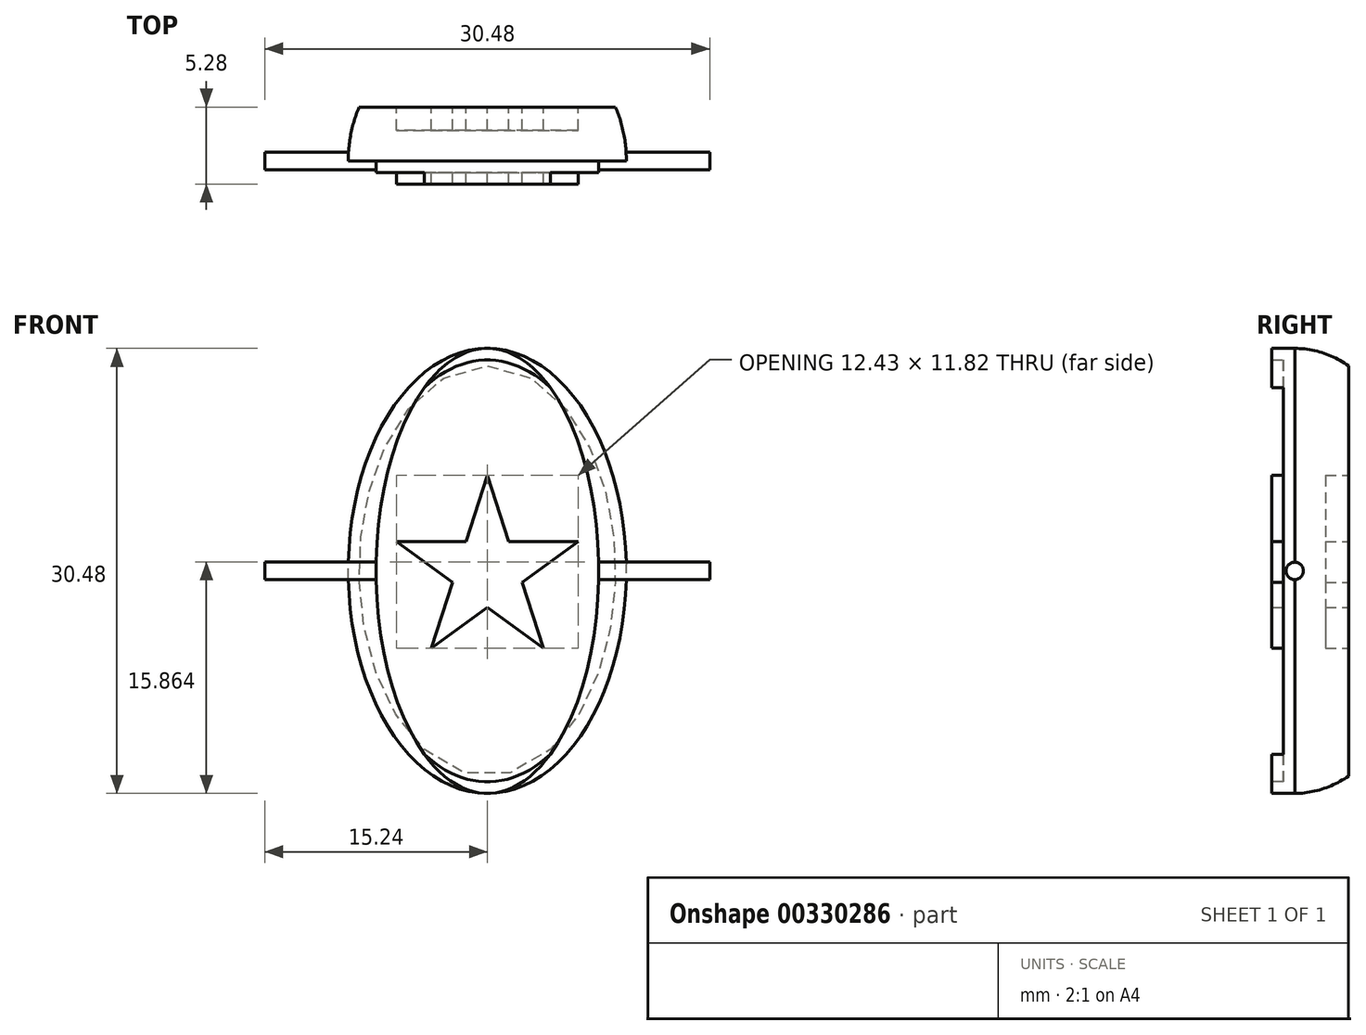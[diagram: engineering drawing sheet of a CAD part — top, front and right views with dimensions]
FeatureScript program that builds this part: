
annotation { "Feature Type Name" : "Feature", "Feature Type Description" : "" }
export const myFeature = defineFeature(function(context is Context, id is Id, definition is map)
    precondition{}
    {
        {
            var Q0;
            Q0=qCreatedBy(makeId("Front.planeOp"),FACE);
            var sketch = newSketch(context, id + "F0", { "sketchPlane" : qUnion([Q0])});
            skEllipticalArc(sketch, "E0", {});
            skLineSegment(sketch, "E1", {"start": v(0, 15.24) * mm, "end": v(0, -15.24) * mm});
            const initialGuessF0  = {"E0": [0, 0, 0, 1, 0.01524, 0.009525, 3.141592653589793, 0]};
            skSetInitialGuess(sketch, initialGuessF0);
            skSolve(sketch);
        }
        {
            var Q0;
            Q0=qSketchRegion(id+"F0",true);
            var Q1;
            Q1=sQuery(id+"F0.wireOp",EDGE,"E1");
            revolve(context, id + "F1", {"entities" : qUnion([Q0]), "axis" : qUnion([Q1]), "revolveType" : RevolveType.ONE_DIRECTION, "oppositeDirection" : true, "angle" : 180 * degree});
        }
        {
            var Q0;
            Q0=qCreatedBy(makeId("Right.planeOp"),FACE);
            var sketch = newSketch(context, id + "F2", { "sketchPlane" : qUnion([Q0])});
            skLineSegment(sketch, "E2.bottom", {"start": v(3.69, 15.9) * mm, "end": v(30.72, 15.9) * mm});
            skLineSegment(sketch, "E2.top", {"start": v(3.69, -22.6) * mm, "end": v(30.72, -22.6) * mm});
            skLineSegment(sketch, "E2.left", {"start": v(3.69, 15.9) * mm, "end": v(3.69, -22.6) * mm});
            skLineSegment(sketch, "E2.right", {"start": v(30.72, 15.9) * mm, "end": v(30.72, -22.6) * mm});
            skSolve(sketch);
        }
        {
            var Q0;
            Q0=qSketchRegion(id+"F2",true);
            extrude(context, id + "F3", {"entities" : qUnion([Q0]), "operationType" : NewBodyOperationType.REMOVE, "oppositeDirection" : true, "depth" : 25.4 * mm, "symmetric" : true});
        }
        {
            var Q0;
            Q0=qCreatedBy(makeId("Right.planeOp"),FACE);
            var sketch = newSketch(context, id + "F4", { "sketchPlane" : qUnion([Q0])});
            skCircle(sketch, "E3", {"center": v(0, 0) * mm, "radius": 0.6 * mm});
            skSolve(sketch);
        }
        {
            var Q0;
            Q0=makeQuery(id+"F1.opRevolve","CAP_FACE",FACE,{"disambiguationData":[OSD([sQuery(id+"F0.wireOp",EDGE,"E0"),sQuery(id+"F0.wireOp",EDGE,"E1")])],"isStart":false});
            var sketch = newSketch(context, id + "F5", { "sketchPlane" : qUnion([Q0])});
            skEllipticalArc(sketch, "E4.0", {});
            skEllipticalArc(sketch, "E4.1", {});
            const initialGuessF5  = {"E4.0": [0, 0, 0, 1, 0.01524, 0.00762, 0, 3.141592653589793], "E4.1": [0, 0, 0, 1, 0.01524, 0.00762, 3.141592653589793, 0]};
            skSetInitialGuess(sketch, initialGuessF5);
            skSolve(sketch);
        }
        {
            var Q0;
            Q0=qSketchRegion(id+"F5",true);
            extrude(context, id + "F6", {"entities" : qUnion([Q0]), "operationType" : NewBodyOperationType.ADD, "depth" : 1.59 * mm});
        }
        {
            var Q0;
            Q0=qSketchRegion(id+"F4",true);
            extrude(context, id + "F7", {"entities" : qUnion([Q0]), "operationType" : NewBodyOperationType.ADD, "depth" : 30.48 * mm, "symmetric" : true});
        }
        {
            var Q0;
            Q0=makeQuery(id+"F6.opExtrude","CAP_FACE",FACE,{"disambiguationData":[OSD([sQuery(id+"F5.wireOp",EDGE,"E4.0"),sQuery(id+"F5.wireOp",EDGE,"E4.1")])],"isStart":false});
            var sketch = newSketch(context, id + "F8", { "sketchPlane" : qUnion([Q0])});
            skEllipse(sketch, "E5", {"center": v(0, 0) * mm, "majorRadius": 14.45 * mm, "minorRadius": 8.73 * mm, "majorAxis": v(0, 1)});
            skSolve(sketch);
        }
        {
            var Q0;
            Q0=qSketchRegion(id+"F8",true);
            extrude(context, id + "F9", {"entities" : qUnion([Q0]), "operationType" : NewBodyOperationType.REMOVE, "oppositeDirection" : true, "depth" : 0.8 * mm});
        }
        {
            var Q0;
            Q0=makeQuery(id+"F9.boolean.opBoolean","COPY",FACE,{"derivedFrom":makeQuery(id+"F9.opExtrude","CAP_FACE",FACE,{"disambiguationData":[OSD([sQuery(id+"F8.wireOp",EDGE,"E5")])],"isStart":false})});
            var sketch = newSketch(context, id + "F10", { "sketchPlane" : qUnion([Q0])});
            skSolve(sketch);
        }
        {
            var Q0;
            Q0=makeQuery(id+"F10.imprint","IMPRINT",FACE,{"disambiguationData":[TD([[makeQuery(id+"F10.imprint","IMPRINT",EDGE,{"derivedFrom":makeQuery(id+"F9.boolean.opBoolean","COPY",EDGE,{"derivedFrom":makeQuery(id+"F9.opExtrude","CAP_EDGE",EDGE,{"disambiguationData":[OSD([sQuery(id+"F8.wireOp",EDGE,"E5")])],"isStart":false})})}),1.0]])]});
            var sketch = newSketch(context, id + "F11", { "sketchPlane" : qUnion([Q0])});
            skLineSegment(sketch, "E6", {"start": v(3.84, -5.29) * mm, "end": v(2.37, -0.77) * mm});
            skLineSegment(sketch, "E7", {"start": v(0, 6.53) * mm, "end": v(-1.47, 2.02) * mm});
            skLineSegment(sketch, "E8", {"start": v(-3.84, -5.29) * mm, "end": v(0, -2.5) * mm});
            skLineSegment(sketch, "E9", {"start": v(6.21, 2.02) * mm, "end": v(1.47, 2.02) * mm});
            skLineSegment(sketch, "E10", {"start": v(-6.21, 2.02) * mm, "end": v(-2.37, -0.77) * mm});
            skLineSegment(sketch, "E11.trimOffspring", {"start": v(-1.47, 2.02) * mm, "end": v(-6.21, 2.02) * mm});
            skLineSegment(sketch, "E12.trimOffspring", {"start": v(-2.37, -0.77) * mm, "end": v(-3.84, -5.29) * mm});
            skLineSegment(sketch, "E13.trimOffspring", {"start": v(0, -2.5) * mm, "end": v(3.84, -5.29) * mm});
            skLineSegment(sketch, "E14.trimOffspring", {"start": v(2.37, -0.77) * mm, "end": v(6.21, 2.02) * mm});
            skLineSegment(sketch, "E15.trimOffspring", {"start": v(1.47, 2.02) * mm, "end": v(0, 6.53) * mm});
            skSolve(sketch);
        }
        {
            var Q0;
            Q0=qSketchRegion(id+"F11",true);
            extrude(context, id + "F12", {"entities" : qUnion([Q0]), "operationType" : NewBodyOperationType.ADD, "depth" : 0.8 * mm});
        }
        {
            var Q0;
            Q0=makeQuery(id+"F3.boolean.opBoolean","COPY",FACE,{"derivedFrom":makeQuery(id+"F3.opExtrude","SWEPT_FACE",FACE,{"disambiguationData":[OSD([sQuery(id+"F2.wireOp",EDGE,"E2.left")])]})});
            var sketch = newSketch(context, id + "F13", { "sketchPlane" : qUnion([Q0])});
            skLineSegment(sketch, "E16.0", {"start": v(2.37, -0.77) * mm, "end": v(3.84, -5.29) * mm});
            skLineSegment(sketch, "E16.1", {"start": v(3.84, -5.29) * mm, "end": v(0, -2.5) * mm});
            skLineSegment(sketch, "E16.2", {"start": v(0, -2.5) * mm, "end": v(-3.84, -5.29) * mm});
            skLineSegment(sketch, "E16.3", {"start": v(-3.84, -5.29) * mm, "end": v(-2.37, -0.77) * mm});
            skLineSegment(sketch, "E16.4", {"start": v(-2.37, -0.77) * mm, "end": v(-6.21, 2.02) * mm});
            skLineSegment(sketch, "E16.5", {"start": v(-6.21, 2.02) * mm, "end": v(-1.47, 2.02) * mm});
            skLineSegment(sketch, "E16.6", {"start": v(-1.47, 2.02) * mm, "end": v(0, 6.53) * mm});
            skLineSegment(sketch, "E16.7", {"start": v(0, 6.53) * mm, "end": v(1.47, 2.02) * mm});
            skLineSegment(sketch, "E16.8", {"start": v(1.47, 2.02) * mm, "end": v(6.21, 2.02) * mm});
            skLineSegment(sketch, "E16.9", {"start": v(6.21, 2.02) * mm, "end": v(2.37, -0.77) * mm});
            skSolve(sketch);
        }
        {
            var Q0;
            Q0=qSketchRegion(id+"F13",true);
            extrude(context, id + "F14", {"entities" : qUnion([Q0]), "operationType" : NewBodyOperationType.REMOVE, "oppositeDirection" : true, "depth" : 1.59 * mm});
        }
    });
